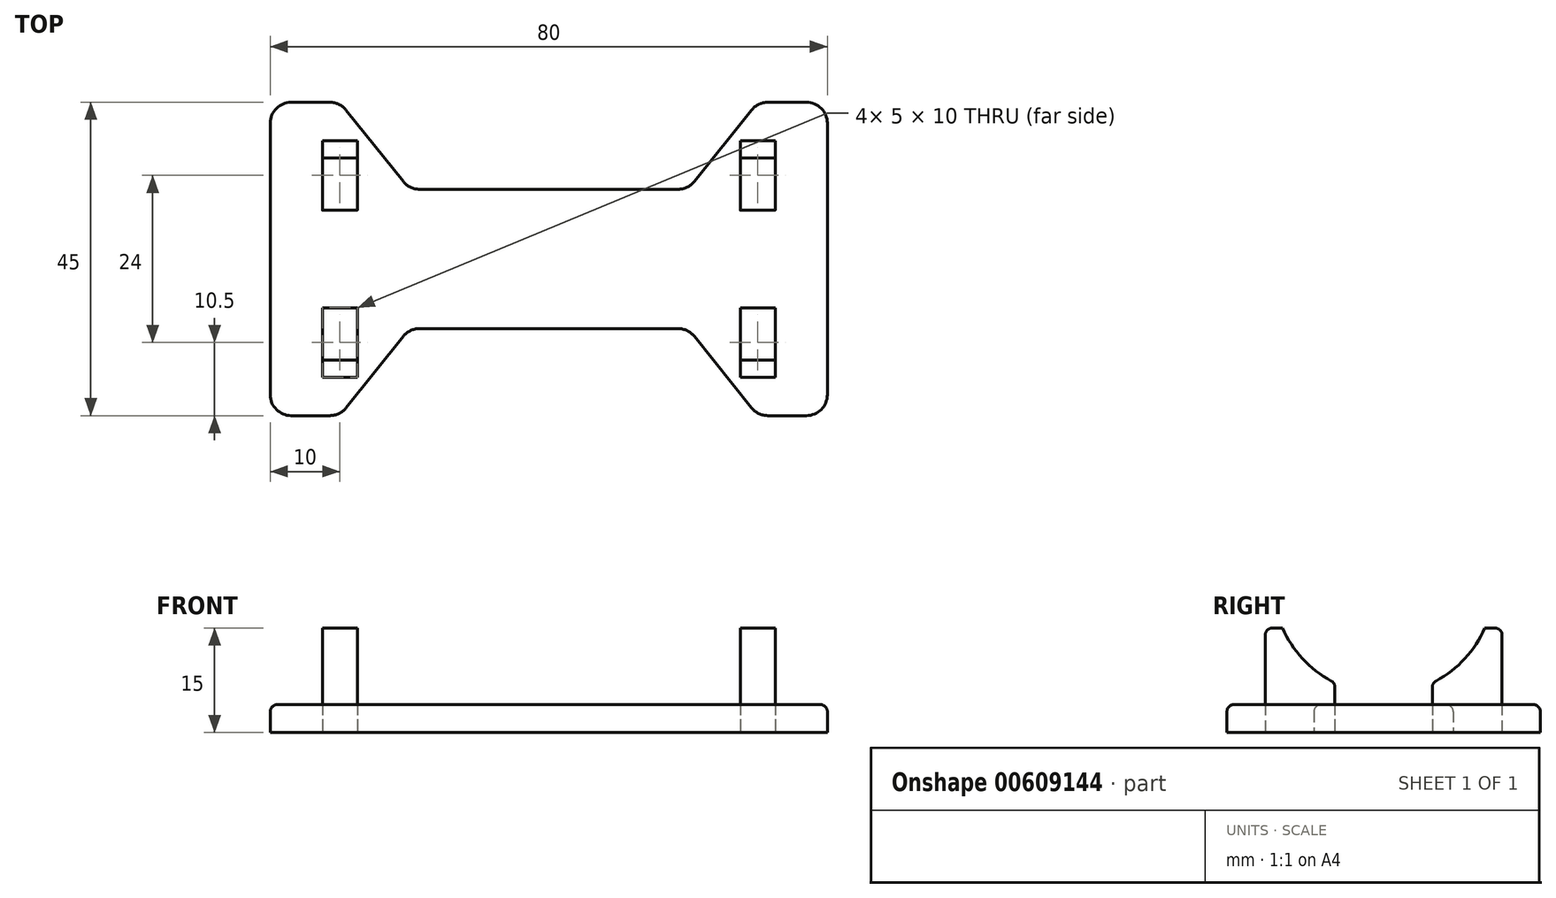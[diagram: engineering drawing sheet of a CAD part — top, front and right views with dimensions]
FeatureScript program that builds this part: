
annotation { "Feature Type Name" : "Feature", "Feature Type Description" : "" }
export const myFeature = defineFeature(function(context is Context, id is Id, definition is map)
    precondition{}
    {
        {
            var Q0;
            Q0=qCreatedBy(makeId("Top.planeOp"),FACE);
            var sketch = newSketch(context, id + "F0", { "sketchPlane" : qUnion([Q0])});
            skLineSegment(sketch, "E0.left", {"start": v(40, 22.5) * mm, "end": v(40, -22.5) * mm});
            skLineSegment(sketch, "E0.right", {"start": v(-40, 22.5) * mm, "end": v(-40, -22.5) * mm});
            skPoint(sketch, "E0.middle", {"position": v(0, 0) * mm});
            skLineSegment(sketch, "E1.bottom", {"start": v(-20, 10) * mm, "end": v(20, 10) * mm});
            skLineSegment(sketch, "E1.top", {"start": v(-20, -10) * mm, "end": v(20, -10) * mm});
            skLineSegment(sketch, "E1.left", {"start": v(-20, 10) * mm, "end": v(-20, -10) * mm});
            skLineSegment(sketch, "E1.right", {"start": v(20, 10) * mm, "end": v(20, -10) * mm});
            skLineSegment(sketch, "E2", {"start": v(-30, 31.62) * mm, "end": v(-30, -45.62) * mm, "construction": true});
            skLineSegment(sketch, "E3", {"start": v(30, 43.08) * mm, "end": v(30, -43.5) * mm, "construction": true});
            skLineSegment(sketch, "E4", {"start": v(-20, 10) * mm, "end": v(-30, 22.5) * mm});
            skLineSegment(sketch, "E5", {"start": v(20, 10) * mm, "end": v(30, 22.5) * mm});
            skLineSegment(sketch, "E6", {"start": v(20, -10) * mm, "end": v(30, -22.5) * mm});
            skLineSegment(sketch, "E7", {"start": v(-20, -10) * mm, "end": v(-30, -22.5) * mm});
            skLineSegment(sketch, "E8", {"start": v(-30, 22.5) * mm, "end": v(-40, 22.5) * mm});
            skLineSegment(sketch, "E9", {"start": v(30, -22.5) * mm, "end": v(40, -22.5) * mm});
            skLineSegment(sketch, "E10", {"start": v(40, 22.5) * mm, "end": v(30, 22.5) * mm});
            skLineSegment(sketch, "E11", {"start": v(-40, -22.5) * mm, "end": v(-30, -22.5) * mm});
            skLineSegment(sketch, "E12.bottom", {"start": v(-50, 17) * mm, "end": v(50, 17) * mm, "construction": true});
            skLineSegment(sketch, "E12.top", {"start": v(-50, -17) * mm, "end": v(50, -17) * mm, "construction": true});
            skLineSegment(sketch, "E12.left", {"start": v(-50, 17) * mm, "end": v(-50, -17) * mm, "construction": true});
            skLineSegment(sketch, "E12.right", {"start": v(50, 17) * mm, "end": v(50, -17) * mm, "construction": true});
            skLineSegment(sketch, "E13.bottom", {"start": v(-32.5, 17) * mm, "end": v(-27.5, 17) * mm});
            skLineSegment(sketch, "E13.top", {"start": v(-32.5, 7) * mm, "end": v(-27.5, 7) * mm});
            skLineSegment(sketch, "E13.left", {"start": v(-32.5, 17) * mm, "end": v(-32.5, 7) * mm});
            skLineSegment(sketch, "E13.right", {"start": v(-27.5, 17) * mm, "end": v(-27.5, 7) * mm});
            skPoint(sketch, "E14.oppositeSnap0", {"position": v(-30, -7) * mm});
            skLineSegment(sketch, "E14.bottom", {"start": v(-32.5, -17) * mm, "end": v(-27.5, -17) * mm});
            skLineSegment(sketch, "E14.top", {"start": v(-32.5, -7) * mm, "end": v(-27.5, -7) * mm});
            skLineSegment(sketch, "E14.left", {"start": v(-32.5, -17) * mm, "end": v(-32.5, -7) * mm});
            skLineSegment(sketch, "E14.right", {"start": v(-27.5, -17) * mm, "end": v(-27.5, -7) * mm});
            skLineSegment(sketch, "E15.bottom", {"start": v(27.5, 17) * mm, "end": v(32.5, 17) * mm});
            skLineSegment(sketch, "E15.top", {"start": v(27.5, 7) * mm, "end": v(32.5, 7) * mm});
            skLineSegment(sketch, "E15.left", {"start": v(27.5, 17) * mm, "end": v(27.5, 7) * mm});
            skLineSegment(sketch, "E15.right", {"start": v(32.5, 17) * mm, "end": v(32.5, 7) * mm});
            skLineSegment(sketch, "E16.bottom", {"start": v(27.5, -17) * mm, "end": v(32.5, -17) * mm});
            skLineSegment(sketch, "E16.top", {"start": v(27.5, -7) * mm, "end": v(32.5, -7) * mm});
            skLineSegment(sketch, "E16.left", {"start": v(27.5, -17) * mm, "end": v(27.5, -7) * mm});
            skLineSegment(sketch, "E16.right", {"start": v(32.5, -17) * mm, "end": v(32.5, -7) * mm});
            skSolve(sketch);
        }
        {
            var Q0;
            Q0=makeQuery(id+"F0.imprint","IMPRINT",FACE,{"disambiguationData":[TD([[makeQuery(id+"F0.imprint","IMPRINT",EDGE,{"derivedFrom":sQuery(id+"F0.wireOp",EDGE,"E13.bottom")}),-1.0]])]});
            var Q1;
            Q1=makeQuery(id+"F0.imprint","IMPRINT",FACE,{"disambiguationData":[TD([[makeQuery(id+"F0.imprint","IMPRINT",EDGE,{"derivedFrom":sQuery(id+"F0.wireOp",EDGE,"E14.bottom")}),1.0]])]});
            var Q2;
            Q2=makeQuery(id+"F0.imprint","IMPRINT",FACE,{"disambiguationData":[TD([[makeQuery(id+"F0.imprint","IMPRINT",EDGE,{"derivedFrom":sQuery(id+"F0.wireOp",EDGE,"E15.bottom")}),-1.0]])]});
            var Q3;
            Q3=makeQuery(id+"F0.imprint","IMPRINT",FACE,{"disambiguationData":[TD([[makeQuery(id+"F0.imprint","IMPRINT",EDGE,{"derivedFrom":sQuery(id+"F0.wireOp",EDGE,"E16.bottom")}),1.0]])]});
            extrude(context, id + "F1", {"entities" : qUnion([Q0, Q1, Q2, Q3]), "depth" : 15 * mm, "offsetDistance" : 25 * mm});
        }
        {
            var Q0;
            Q0 = qSketchRegion(id + "F0", true);
            extrude(context, id + "F2", {"entities" : qUnion([Q0]), "depth" : 4 * mm, "offsetDistance" : 25 * mm});
        }
        {
            var Q0;
            Q0=makeQuery(id+"F2.opExtrude","SWEPT_EDGE",EDGE,{"disambiguationData":[OSD([sQuery(id+"F0.wireOp",EDGE,"E8"),sQuery(id+"F0.wireOp",EDGE,"E0.right")])]});
            var Q1;
            Q1=makeQuery(id+"F2.opExtrude","SWEPT_EDGE",EDGE,{"disambiguationData":[OSD([sQuery(id+"F0.wireOp",EDGE,"E0.right"),sQuery(id+"F0.wireOp",EDGE,"E11")])]});
            var Q2;
            Q2=makeQuery(id+"F2.opExtrude","SWEPT_EDGE",EDGE,{"disambiguationData":[OSD([sQuery(id+"F0.wireOp",EDGE,"E0.left"),sQuery(id+"F0.wireOp",EDGE,"E9")])]});
            var Q3;
            Q3=makeQuery(id+"F2.opExtrude","SWEPT_EDGE",EDGE,{"disambiguationData":[OSD([sQuery(id+"F0.wireOp",EDGE,"E0.left"),sQuery(id+"F0.wireOp",EDGE,"E10")])]});
            var Q4;
            Q4=makeQuery(id+"F2.opExtrude","SWEPT_EDGE",EDGE,{"disambiguationData":[OSD([sQuery(id+"F0.wireOp",EDGE,"E4"),sQuery(id+"F0.wireOp",EDGE,"E8")])]});
            var Q5;
            Q5=makeQuery(id+"F2.opExtrude","SWEPT_EDGE",EDGE,{"disambiguationData":[OSD([sQuery(id+"F0.wireOp",EDGE,"E5"),sQuery(id+"F0.wireOp",EDGE,"E10")])]});
            var Q6;
            Q6=makeQuery(id+"F2.opExtrude","SWEPT_EDGE",EDGE,{"disambiguationData":[OSD([sQuery(id+"F0.wireOp",EDGE,"E6"),sQuery(id+"F0.wireOp",EDGE,"E9")])]});
            var Q7;
            Q7=makeQuery(id+"F2.opExtrude","SWEPT_EDGE",EDGE,{"disambiguationData":[OSD([sQuery(id+"F0.wireOp",EDGE,"E7"),sQuery(id+"F0.wireOp",EDGE,"E11")])]});
            var Q8;
            Q8=makeQuery(id+"F2.opExtrude","SWEPT_EDGE",EDGE,{"disambiguationData":[OSD([sQuery(id+"F0.wireOp",EDGE,"E1.top"),sQuery(id+"F0.wireOp",EDGE,"E1.left"),sQuery(id+"F0.wireOp",EDGE,"E7")])]});
            var Q9;
            Q9=makeQuery(id+"F2.opExtrude","SWEPT_EDGE",EDGE,{"disambiguationData":[OSD([sQuery(id+"F0.wireOp",EDGE,"E1.bottom"),sQuery(id+"F0.wireOp",EDGE,"E1.left"),sQuery(id+"F0.wireOp",EDGE,"E4")])]});
            var Q10;
            Q10=makeQuery(id+"F2.opExtrude","SWEPT_EDGE",EDGE,{"disambiguationData":[OSD([sQuery(id+"F0.wireOp",EDGE,"E1.top"),sQuery(id+"F0.wireOp",EDGE,"E1.right"),sQuery(id+"F0.wireOp",EDGE,"E6")])]});
            var Q11;
            Q11=makeQuery(id+"F2.opExtrude","SWEPT_EDGE",EDGE,{"disambiguationData":[OSD([sQuery(id+"F0.wireOp",EDGE,"E1.bottom"),sQuery(id+"F0.wireOp",EDGE,"E1.right"),sQuery(id+"F0.wireOp",EDGE,"E5")])]});
            fillet(context, id + "F3", {"entities" : qUnion([Q0, Q1, Q2, Q3, Q4, Q5, Q6, Q7, Q8, Q9, Q10, Q11]), "radius" : 3 * mm, "tangentPropagation" : true, "allowEdgeOverflow" : false});
        }
        {
            var Q0;
            Q0=makeQuery(id+"F1.opExtrude","SWEPT_FACE",FACE,{"disambiguationData":[OSD([sQuery(id+"F0.wireOp",EDGE,"E16.right")])]});
            var sketch = newSketch(context, id + "F4", { "sketchPlane" : qUnion([Q0])});
            skCircle(sketch, "E17", {"center": v(0, 21.35) * mm, "radius": 15.85 * mm});
            skLineSegment(sketch, "E18", {"start": v(-12, 0) * mm, "end": v(-12, 54.96) * mm, "construction": true});
            skSolve(sketch);
        }
        {
            var Q0;
            {var subQ0=sQuery(id+"F4.wireOp",EDGE,"E17");var subQ1=sQuery(id+"F0.wireOp",EDGE,"E16.right");var subQ4=makeQuery(id+"F1.opExtrude","CAP_EDGE",EDGE,{"disambiguationData":[OSD([subQ1])],"isStart":false});var subQ5=makeQuery(id+"F4.imprint","INTERSECT",VERTEX,{"derivedFrom":[subQ4,subQ0]});Q0=makeQuery(id+"F4.imprint","IMPRINT",FACE,{"disambiguationData":[TD([[makeQuery(id+"F4.imprint","IMPRINT",EDGE,{"disambiguationData":[TD([[subQ5,1.0]])],"derivedFrom":subQ0}),1.0]])]});}
            var Q1;
            {var subQ0=sQuery(id+"F4.wireOp",EDGE,"E17");var subQ1=sQuery(id+"F0.wireOp",EDGE,"E16.right");var subQ4=makeQuery(id+"F1.opExtrude","CAP_EDGE",EDGE,{"disambiguationData":[OSD([subQ1])],"isStart":false});var subQ5=makeQuery(id+"F4.imprint","INTERSECT",VERTEX,{"derivedFrom":[subQ4,subQ0]});Q1=makeQuery(id+"F4.imprint","IMPRINT",FACE,{"disambiguationData":[TD([[makeQuery(id+"F4.imprint","IMPRINT",EDGE,{"disambiguationData":[TD([[subQ5,-1.0]])],"derivedFrom":subQ0}),1.0]])]});}
            extrude(context, id + "F5", {"entities" : qUnion([Q0, Q1]), "operationType" : NewBodyOperationType.REMOVE, "oppositeDirection" : true, "depth" : 5 * mm, "offsetDistance" : 25 * mm});
        }
        {
            var Q0;
            Q0=makeQuery(id+"F1.opExtrude","SWEPT_FACE",FACE,{"disambiguationData":[OSD([sQuery(id+"F0.wireOp",EDGE,"E13.left")])]});
            var sketch = newSketch(context, id + "F6", { "sketchPlane" : qUnion([Q0])});
            skLineSegment(sketch, "E19", {"start": v(-12, 0) * mm, "end": v(-12, 46) * mm, "construction": true});
            skCircle(sketch, "E20", {"center": v(0, 21.35) * mm, "radius": 15.85 * mm});
            skSolve(sketch);
        }
        {
            var Q0;
            Q0 = qSketchRegion(id + "F6", true);
            extrude(context, id + "F7", {"entities" : qUnion([Q0]), "operationType" : NewBodyOperationType.REMOVE, "oppositeDirection" : true, "depth" : 5 * mm, "offsetDistance" : 25 * mm});
        }
        {
            var Q0;
            Q0=makeQuery(id+"F1.opExtrude","CAP_EDGE",EDGE,{"disambiguationData":[OSD([sQuery(id+"F0.wireOp",EDGE,"E13.bottom")])],"isStart":false});
            var Q1;
            Q1=makeQuery(id+"F1.opExtrude","CAP_EDGE",EDGE,{"disambiguationData":[OSD([sQuery(id+"F0.wireOp",EDGE,"E15.bottom")])],"isStart":false});
            var Q2;
            Q2=makeQuery(id+"F1.opExtrude","CAP_EDGE",EDGE,{"disambiguationData":[OSD([sQuery(id+"F0.wireOp",EDGE,"E14.bottom")])],"isStart":false});
            var Q3;
            Q3=makeQuery(id+"F1.opExtrude","CAP_EDGE",EDGE,{"disambiguationData":[OSD([sQuery(id+"F0.wireOp",EDGE,"E16.bottom")])],"isStart":false});
            var Q4;
            Q4=makeQuery(id+"F7.boolean.opBoolean","INTERSECT",EDGE,{"derivedFrom":[makeQuery(id+"F1.opExtrude","SWEPT_FACE",FACE,{"disambiguationData":[OSD([sQuery(id+"F0.wireOp",EDGE,"E13.top")])]}),makeQuery(id+"F7.opExtrude","SWEPT_FACE",FACE,{"disambiguationData":[OSD([sQuery(id+"F6.wireOp",EDGE,"E20")])]})]});
            var Q5;
            Q5=makeQuery(id+"F5.boolean.opBoolean","INTERSECT",EDGE,{"derivedFrom":[makeQuery(id+"F1.opExtrude","SWEPT_FACE",FACE,{"disambiguationData":[OSD([sQuery(id+"F0.wireOp",EDGE,"E15.top")])]}),makeQuery(id+"F5.opExtrude","SWEPT_FACE",FACE,{"disambiguationData":[OSD([sQuery(id+"F4.wireOp",EDGE,"E17")])]})]});
            var Q6;
            Q6=makeQuery(id+"F5.boolean.opBoolean","INTERSECT",EDGE,{"derivedFrom":[makeQuery(id+"F1.opExtrude","SWEPT_FACE",FACE,{"disambiguationData":[OSD([sQuery(id+"F0.wireOp",EDGE,"E16.top")])]}),makeQuery(id+"F5.opExtrude","SWEPT_FACE",FACE,{"disambiguationData":[OSD([sQuery(id+"F4.wireOp",EDGE,"E17")])]})]});
            var Q7;
            Q7=makeQuery(id+"F7.boolean.opBoolean","INTERSECT",EDGE,{"derivedFrom":[makeQuery(id+"F1.opExtrude","SWEPT_FACE",FACE,{"disambiguationData":[OSD([sQuery(id+"F0.wireOp",EDGE,"E14.top")])]}),makeQuery(id+"F7.opExtrude","SWEPT_FACE",FACE,{"disambiguationData":[OSD([sQuery(id+"F6.wireOp",EDGE,"E20")])]})]});
            fillet(context, id + "F8", {"entities" : qUnion([Q0, Q1, Q2, Q3, Q4, Q5, Q6, Q7]), "radius" : 1 * mm, "tangentPropagation" : true, "allowEdgeOverflow" : false});
        }
        {
            var Q0;
            Q0=makeQuery(id+"F2.opExtrude","CAP_EDGE",EDGE,{"disambiguationData":[OSD([sQuery(id+"F0.wireOp",EDGE,"E1.bottom")])],"isStart":false});
            fillet(context, id + "F9", {"entities" : qUnion([Q0]), "radius" : 1 * mm, "tangentPropagation" : true, "allowEdgeOverflow" : false});
        }
    });
